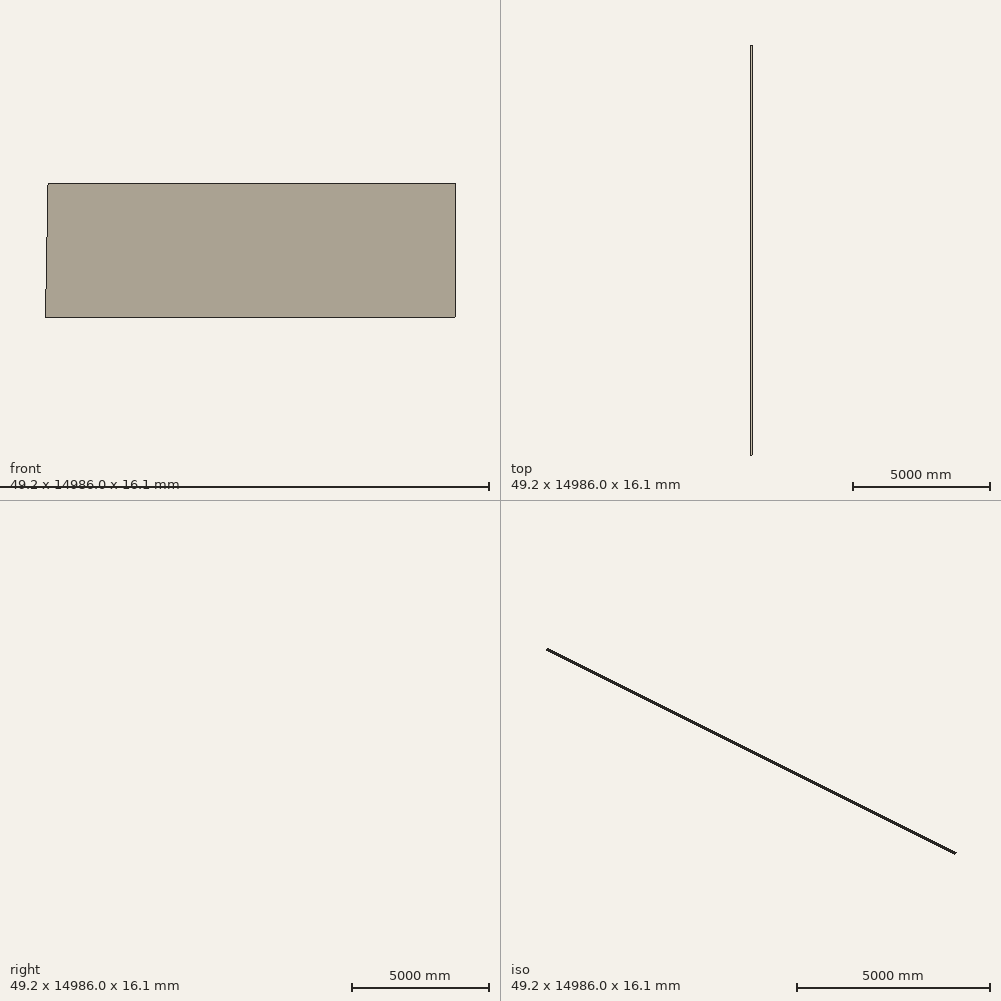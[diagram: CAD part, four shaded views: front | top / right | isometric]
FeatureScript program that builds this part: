
annotation { "Feature Type Name" : "Feature", "Feature Type Description" : "" }
export const myFeature = defineFeature(function(context is Context, id is Id, definition is map)
    precondition{}
    {
        {
            var Q0;
            Q0=qCreatedBy(makeId("Front.planeOp"),FACE);
            var sketch = newSketch(context, id + "F0", { "sketchPlane" : qUnion([Q0])});
            skLineSegment(sketch, "E0", {"start": v(-43.95, 21.82) * mm, "end": v(5.26, 21.82) * mm});
            skLineSegment(sketch, "E1", {"start": v(5.26, 21.82) * mm, "end": v(5.26, 37.92) * mm});
            skLineSegment(sketch, "E2", {"start": v(5.26, 37.92) * mm, "end": v(-43.64, 37.92) * mm});
            skLineSegment(sketch, "E3", {"start": v(-43.64, 37.92) * mm, "end": v(-43.95, 21.82) * mm});
            skSolve(sketch);
        }
        {
            var Q0;
            Q0=makeQuery(id+"F0.imprint","IMPRINT",FACE,{"disambiguationData":[TD([[makeQuery(id+"F0.imprint","IMPRINT",EDGE,{"derivedFrom":sQuery(id+"F0.wireOp",EDGE,"E0")}),1.0]])]});
            extrude(context, id + "F1", {"entities" : qUnion([Q0]), "depth" : 14986 * mm});
        }
    });
